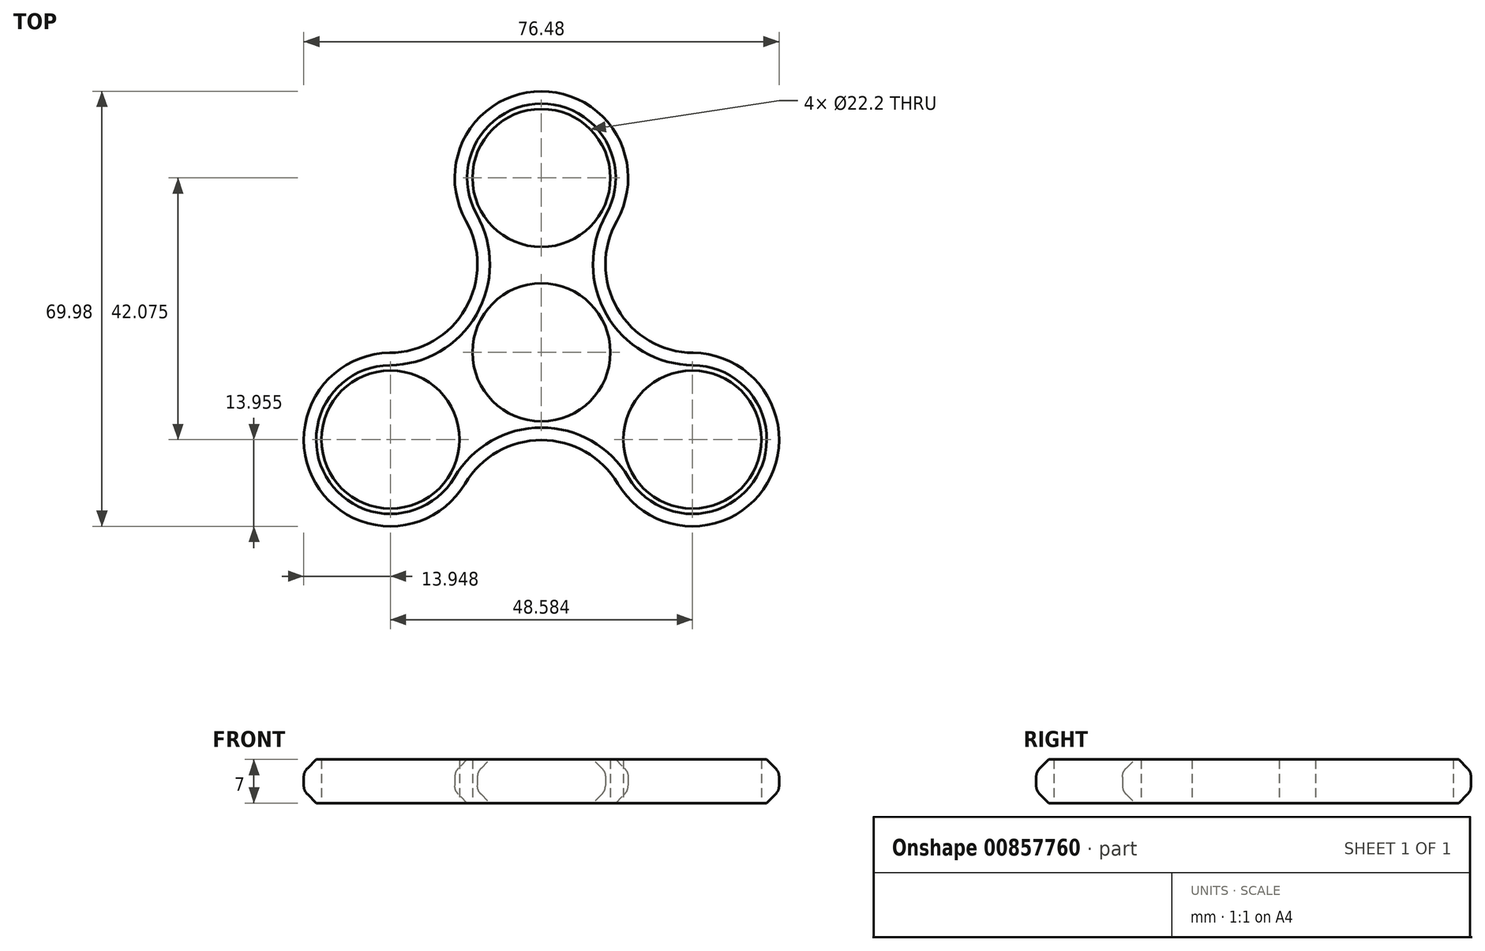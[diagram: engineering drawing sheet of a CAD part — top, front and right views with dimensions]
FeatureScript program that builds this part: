
annotation { "Feature Type Name" : "Feature", "Feature Type Description" : "" }
export const myFeature = defineFeature(function(context is Context, id is Id, definition is map)
    precondition{}
    {
        {
            var Q0;
            Q0=qCreatedBy(makeId("Top.planeOp"),FACE);
            var sketch = newSketch(context, id + "F0", { "sketchPlane" : qUnion([Q0])});
            skCircle(sketch, "E0", {"center": v(0, 0) * mm, "radius": 11.1 * mm});
            skCircle(sketch, "E1.0", {"center": v(0, 0) * mm, "radius": 14.1 * mm, "construction": true});
            skCircle(sketch, "E2", {"center": v(0, 28.05) * mm, "radius": 11.1 * mm});
            skArc(sketch, "E3.0", {"start": v(12.15, 21.19) * mm, "mid": v(0, 42) * mm, "end": v(-12.15, 21.19) * mm});
            skCircle(sketch, "E4.1.0", {"center": v(-24.3, -14.02) * mm, "radius": 11.1 * mm});
            skCircle(sketch, "E4.2.0", {"center": v(24.3, -14.02) * mm, "radius": 11.1 * mm});
            skArc(sketch, "E4.2.1", {"start": v(12.28, -21.11) * mm, "mid": v(36.37, -21) * mm, "end": v(24.42, -0.08) * mm});
            skArc(sketch, "E5", {"start": v(12.28, -21.11) * mm, "mid": v(0, -14.1) * mm, "end": v(-12.28, -21.11) * mm});
            skArc(sketch, "E6.1.0", {"start": v(12.15, 21.19) * mm, "mid": v(12.21, 7.05) * mm, "end": v(24.42, -0.08) * mm});
            skArc(sketch, "E6.2.0", {"start": v(-24.42, -0.08) * mm, "mid": v(-12.21, 7.05) * mm, "end": v(-12.15, 21.19) * mm});
            skArc(sketch, "E7", {"start": v(-24.42, -0.08) * mm, "mid": v(-36.37, -21) * mm, "end": v(-12.28, -21.11) * mm});
            skSolve(sketch);
        }
        {
            var Q0;
            Q0=makeQuery(id+"F0.imprint","IMPRINT",FACE,{"disambiguationData":[TD([[makeQuery(id+"F0.imprint","IMPRINT",EDGE,{"derivedFrom":sQuery(id+"F0.wireOp",EDGE,"E0")}),-1.0]])]});
            extrude(context, id + "F1", {"entities" : qUnion([Q0]), "depth" : 7 * mm, "offsetDistance" : 25 * mm});
        }
        {
            var Q0;
            Q0=makeQuery(id+"F1.opExtrude","CAP_EDGE",EDGE,{"disambiguationData":[OSD([sQuery(id+"F0.wireOp",EDGE,"E7")])],"isStart":true});
            var Q1;
            Q1=makeQuery(id+"F1.opExtrude","CAP_EDGE",EDGE,{"disambiguationData":[OSD([sQuery(id+"F0.wireOp",EDGE,"E7")])],"isStart":false});
            chamfer(context, id + "F2", {"entities" : qUnion([Q0, Q1]), "chamferType" : ChamferType.OFFSET_ANGLE, "width" : 2 * mm, "oppositeDirection" : false, "angle" : 45 * degree, "tangentPropagation" : true});
        }
        {
            var Q0;
            {var subQ0=sQuery(id+"F0.wireOp",EDGE,"E5");Q0=makeQuery(id+"F2.opChamfer","BLEND_EDGE",EDGE,{"blendedFrom":[makeQuery(id+"F1.opExtrude","CAP_EDGE",EDGE,{"disambiguationData":[OSD([subQ0])],"isStart":true}),makeQuery(id+"F1.opExtrude","SWEPT_FACE",FACE,{"disambiguationData":[OSD([subQ0])]})],"blendedInto":[makeQuery(id+"F1.opExtrude","SWEPT_FACE",FACE,{"disambiguationData":[OSD([subQ0])]})]});}
            var Q1;
            {var subQ0=sQuery(id+"F0.wireOp",EDGE,"E5");Q1=makeQuery(id+"F2.opChamfer","BLEND_EDGE",EDGE,{"blendedFrom":[makeQuery(id+"F1.opExtrude","CAP_EDGE",EDGE,{"disambiguationData":[OSD([subQ0])],"isStart":false}),makeQuery(id+"F1.opExtrude","SWEPT_FACE",FACE,{"disambiguationData":[OSD([subQ0])]})],"blendedInto":[makeQuery(id+"F1.opExtrude","SWEPT_FACE",FACE,{"disambiguationData":[OSD([subQ0])]})]});}
            fillet(context, id + "F3", {"entities" : qUnion([Q0, Q1]), "radius" : 2 * mm, "tangentPropagation" : true, "allowEdgeOverflow" : false});
        }
    });
